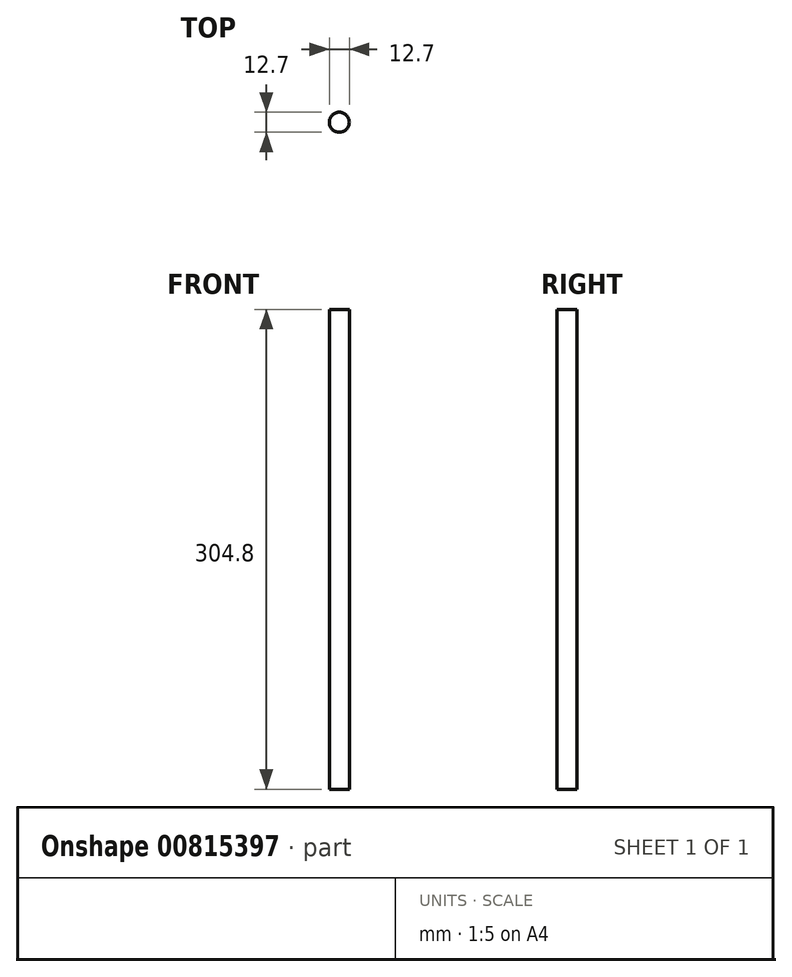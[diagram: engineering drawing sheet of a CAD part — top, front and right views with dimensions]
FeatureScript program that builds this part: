
annotation { "Feature Type Name" : "Feature", "Feature Type Description" : "" }
export const myFeature = defineFeature(function(context is Context, id is Id, definition is map)
    precondition{}
    {
        {
            var Q0;
            Q0=qCreatedBy(makeId("Top.planeOp"),FACE);
            var sketch = newSketch(context, id + "F0", { "sketchPlane" : qUnion([Q0])});
            skCircle(sketch, "E0", {"center": v(0, 0) * mm, "radius": 6.35 * mm});
            skSolve(sketch);
        }
        {
            var Q0;
            Q0=qSketchRegion(id+"F0",true);
            extrude(context, id + "F1", {"entities" : qUnion([Q0]), "depth" : 304.8 * mm});
        }
    });
